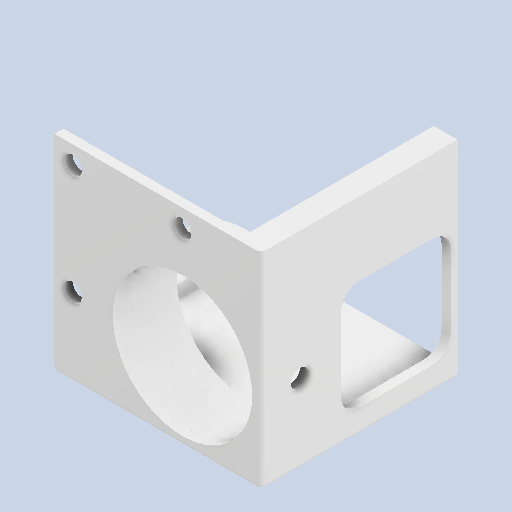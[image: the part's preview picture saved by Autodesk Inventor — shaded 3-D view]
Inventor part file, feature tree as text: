
AUTODESK INVENTOR PART (.ipt)
format: ipt  version: 2023 (Build 270158000, 158)  size: 242,176 bytes
history: native  units: in
note: dims shown in document units (in); Inventor stores cm internally (conversion verified against a paired STEP export)
features: extrude x5, sketch x3, fillet x2, hole x1
ambient origin geometry x8: Origin, YZ Plane, XZ Plane, XY Plane, X Axis, Y Axis, Z Axis, Center Point
bodies: Solid1 (feature_tree)
feature tree (11):
  sketch  "Sketch1"  dims[d0=1.1811in d1=0.4724in]
  extrude  "Extrusion1"  Depth=0.4724in
  hole  "Hole1"  [1 undecoded]
  extrude  "Extrusion5"  Depth=1.5748in
  fillet  "Fillet1"  Radius=1.7795in
  extrude  "Extrusion8"  Depth=1.7795in
  extrude  "Extrusion12"  Depth=0.1575in
  extrude  "Extrusion14"  Depth=0.0787in TaperAngle=0.0deg
  fillet  "Fillet2"  Radius=0.1575in
  sketch  "Sketch2"  dims[d2=1.5748in d3=0.4724in]
  sketch  "Sketch5"  dims[d4=1.5748in d5=1.5748in d6=1.7795in d7=1.7795in d8=1.2008in d9=0.0787in d10=0.0in d11=0.1575in d12=0.1575in d13=0.9449in d14=0.9449in d15=0.1575in d16=0.2362in d17=0.1575in d18=0.0787in d19=90.0deg d20=0.315in d21=0.8108in d22=0.0787in d30=0.063in d33=0.0787in d34=0.0787in d35=0.0787in d36=1.6142in d37=0.0in d42=0.0394in d43=0.0787in d44=0.0787in d45=1.6142in d46=0.0in d56=0.4724in d57=0.0in d64=1.1024in d65=0.5315in d66=0.2559in d67=0.1575in d71=0.1181in d72=0.0in d73=0.1575in d31=0.0197in d32=0.0344in d38=0.0197in d39=0.0344in]
note: 1 required parameter value undecoded (feature->parameter linkage not recoverable at this tier; creation-order binding heuristic only, values carry confidence <= 0.55)
